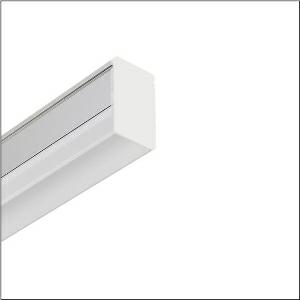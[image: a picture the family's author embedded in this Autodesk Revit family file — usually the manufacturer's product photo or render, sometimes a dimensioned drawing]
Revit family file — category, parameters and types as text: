
# Revit family: batten_41-f_51lp327dm10af
name_source: partatom
category: Lighting Fixtures
units: mm (PartAtom-declared; Revit-internal decimal feet)

## family parameters
Cut with Voids When Loaded = No
Host = Face
Light Source = No
Part Type = Normal
Room Calculation Point = No
Round Connector Dimension = Use Diameter
Shared = No

## types (1)
- --- (1 x LED, 1000 lm, 8.3 W, 5000K)
    Apparent Load = 8 VA
    CIE Flux Codes = 39 68 88 89 100
    Color Rendering = 80
    Color Temperature = 5000K
    Default Elevation = 1800 mm
    Description = Batten 41-F, batten luminaire, primary optical cover: cover, of PC, frosted, light emission: direct distribution, primary light characteristic: symmetric, installation type: surface-mounted, LED, rated luminous flux: 1.000lm, luminous efficacy: 120lm/W, light colour: 830/840/850, colour temperature: 3000/4000/5000K, control gear: ON/OFF, with terminal, 2-pole, mains connection: 220..240V, AC, 50/60Hz, rated input power: 8.3W, housing, of aluminium, silver, length: 580mm, width: 25mm, height: 44mm, end cap, of PC, white, protection rating (complete): IP20, insulation class (complete): insulation class II (safety insulation), certification: CE, permissible operating ambient temperature: -20..+40°C, packaging unit: 1 piece
    Height = 44 mm
    Lamp = 1 x LED
    Lamp Light Flux = 1000 lm
    Lamp Power = 8.3 W
    Lamp count = 1
    Length = 580 mm
    Luminous efficacy = 120 lm/W
    Manufacturer = Siteco
    ModVariant = No
    Model = 51LP327DM10AF
    Mounting Place = Ceiling
    Mounting Type = Surface mounted
    Number of Poles = 1
    OnlyDefault = Yes
    Power Factor = 1
    Product Name = Batten 41-F
    Product group = batten luminaire
    ProductGroupID = 303
    Protection Class = Protection class II
    Protection Degree = IP 20
    RLX_Detail_Level = 1
    RLX_Emergency_Light_Flux = 0 lm
    RLX_Emergency_Type = 0
    RLX_Emergency_Type_DB = No
    RlxData = <blob elided: 27917 chars, md5=079f4e84>
    Socket = socket
    Standby Power = 0 W
    System Light Flux = 1000 lm
    System Power = 8 W
    Type Comments = individual setting: colour temperature 5000K
    Type Image = l_1007255.jpg
    URL = http://relux.com
    VarID = @adj_022804
    Voltage = 0 V
    Weight = 0.00 kg
    Width = 25 mm  [stored 0.082021 ft]

note: [stored X ft] marks values corroborated as IEEE doubles in the binary element streams (Revit-internal decimal feet)

## geometry (parser evidence)
native form markers: Blend x4, Sweep x12
no freeform markers — native parametric forms only
